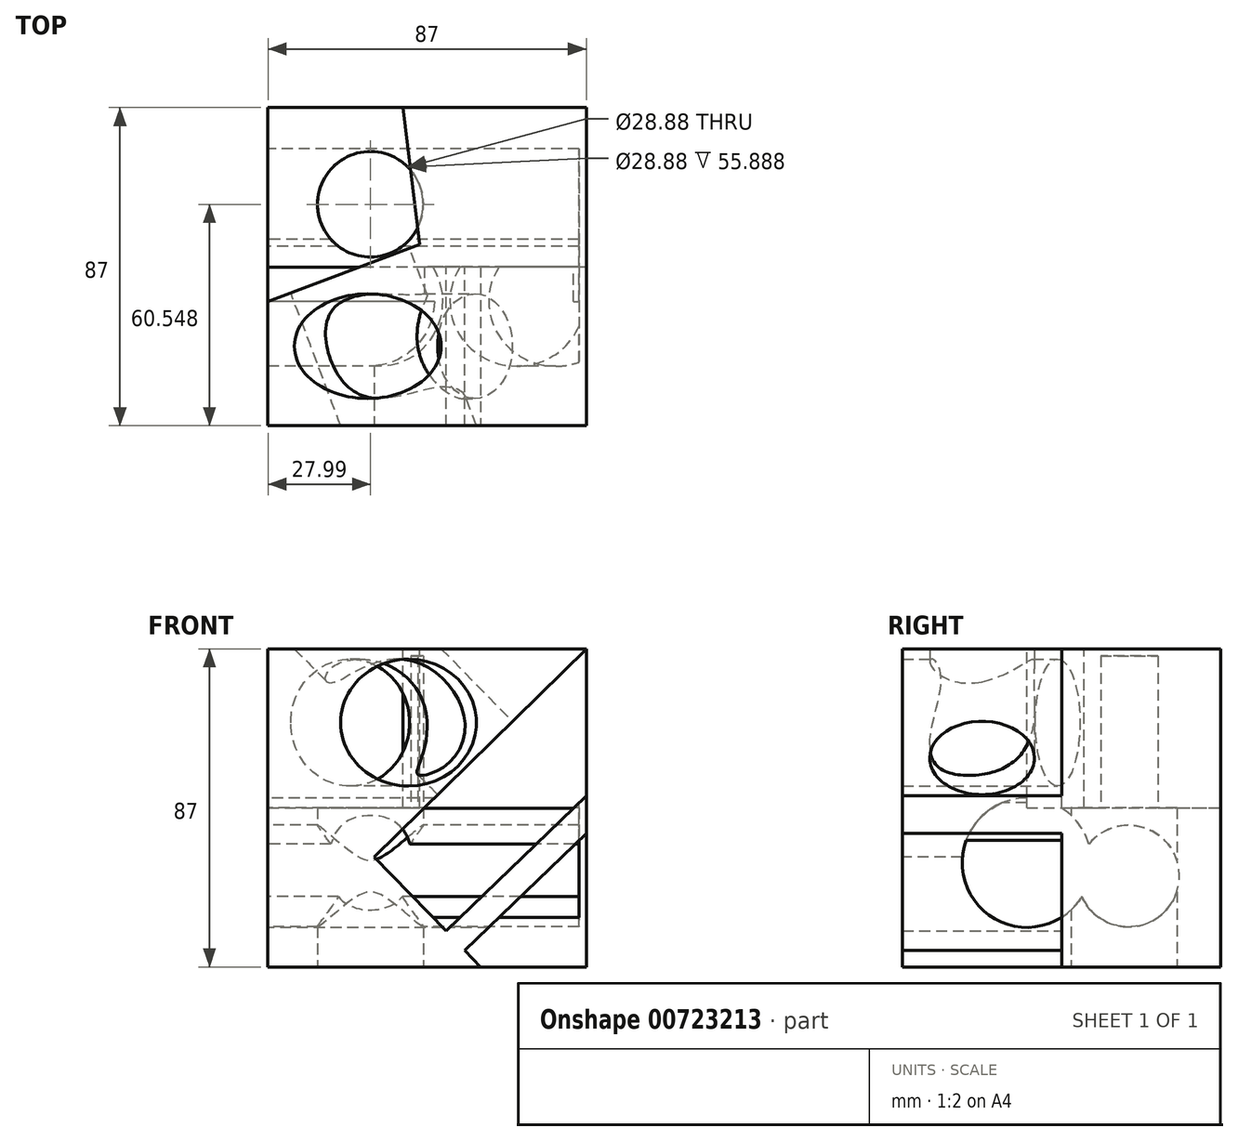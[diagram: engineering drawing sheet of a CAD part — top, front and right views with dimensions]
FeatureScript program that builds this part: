
annotation { "Feature Type Name" : "Feature", "Feature Type Description" : "" }
export const myFeature = defineFeature(function(context is Context, id is Id, definition is map)
    precondition{}
    {
        {
            var Q0;
            Q0=qCreatedBy(makeId("Front.planeOp"),FACE);
            var sketch = newSketch(context, id + "F0", { "sketchPlane" : qUnion([Q0])});
            skLineSegment(sketch, "E0.bottom", {"start": v(-41.52, 43.5) * mm, "end": v(45.48, 43.5) * mm});
            skLineSegment(sketch, "E0.top", {"start": v(-41.52, -43.5) * mm, "end": v(45.48, -43.5) * mm});
            skLineSegment(sketch, "E0.left", {"start": v(-41.52, 43.5) * mm, "end": v(-41.52, -43.5) * mm});
            skLineSegment(sketch, "E0.right", {"start": v(45.48, 43.5) * mm, "end": v(45.48, -43.5) * mm});
            skPoint(sketch, "E0.middle", {"position": v(1.98, 0) * mm});
            skSolve(sketch);
        }
        {
            var Q0;
            Q0=makeQuery(id+"F0.imprint","IMPRINT",FACE,{"disambiguationData":[TD([[makeQuery(id+"F0.imprint","IMPRINT",EDGE,{"derivedFrom":sQuery(id+"F0.wireOp",EDGE,"E0.bottom")}),-1.0]])]});
            extrude(context, id + "F1", {"entities" : qUnion([Q0]), "depth" : 87 * mm, "offsetDistance" : 25 * mm});
        }
        {
            var Q0;
            Q0=makeQuery(id+"F1.opExtrude","SWEPT_FACE",FACE,{"disambiguationData":[OSD([sQuery(id+"F0.wireOp",EDGE,"E0.bottom")])]});
            var sketch = newSketch(context, id + "F2", { "sketchPlane" : qUnion([Q0])});
            skLineSegment(sketch, "E1", {"start": v(-41.52, -53.03) * mm, "end": v(45.48, -20.33) * mm});
            skLineSegment(sketch, "E2", {"start": v(0, -37.42) * mm, "end": v(-4.6, 0) * mm});
            skSolve(sketch);
        }
        {
            var Q0;
            {var subQ4=sQuery(id+"F2.wireOp",EDGE,"E2");Q0=makeQuery(id+"F2.imprint","IMPRINT",FACE,{"disambiguationData":[TD([[makeQuery(id+"F2.imprint","IMPRINT",EDGE,{"derivedFrom":subQ4}),1.0]])]});}
            extrude(context, id + "F3", {"entities" : qUnion([Q0]), "operationType" : NewBodyOperationType.REMOVE, "oppositeDirection" : true, "depth" : 43.5 * mm, "offsetDistance" : 25 * mm});
        }
        {
            var Q0;
            Q0=makeQuery(id+"F1.opExtrude","CAP_FACE",FACE,{"disambiguationData":[OSD([sQuery(id+"F0.wireOp",EDGE,"E0.bottom"),sQuery(id+"F0.wireOp",EDGE,"E0.top"),sQuery(id+"F0.wireOp",EDGE,"E0.left"),sQuery(id+"F0.wireOp",EDGE,"E0.right")])],"isStart":false});
            var sketch = newSketch(context, id + "F4", { "sketchPlane" : qUnion([Q0])});
            skLineSegment(sketch, "E3", {"start": v(-41.52, 16.7) * mm, "end": v(16.6, -43.5) * mm});
            skLineSegment(sketch, "E4", {"start": v(-12.46, -13.4) * mm, "end": v(45.48, 43.5) * mm});
            skSolve(sketch);
        }
        {
            var Q0;
            {var subQ3=sQuery(id+"F4.wireOp",EDGE,"E4");Q0=makeQuery(id+"F4.imprint","IMPRINT",FACE,{"disambiguationData":[TD([[makeQuery(id+"F4.imprint","IMPRINT",EDGE,{"derivedFrom":subQ3}),-1.0]])]});}
            extrude(context, id + "F5", {"entities" : qUnion([Q0]), "operationType" : NewBodyOperationType.REMOVE, "oppositeDirection" : true, "depth" : 43.5 * mm, "offsetDistance" : 25 * mm});
        }
        {
            var Q0;
            Q0=makeQuery(id+"F1.opExtrude","SWEPT_FACE",FACE,{"disambiguationData":[OSD([sQuery(id+"F0.wireOp",EDGE,"E0.top")])]});
            var sketch = newSketch(context, id + "F6", { "sketchPlane" : qUnion([Q0])});
            skCircle(sketch, "E5", {"center": v(-13.53, 26.45) * mm, "radius": 14.44 * mm});
            skSolve(sketch);
        }
        {
            var Q0;
            Q0=makeQuery(id+"F6.imprint","IMPRINT",FACE,{"disambiguationData":[TD([[makeQuery(id+"F6.imprint","IMPRINT",EDGE,{"derivedFrom":sQuery(id+"F6.wireOp",EDGE,"E5")}),1.0]])]});
            extrude(context, id + "F7", {"entities" : qUnion([Q0]), "operationType" : NewBodyOperationType.REMOVE, "oppositeDirection" : true, "depth" : 85 * mm, "offsetDistance" : 25 * mm});
        }
        {
            var Q0;
            Q0=makeQuery(id+"F1.opExtrude","SWEPT_FACE",FACE,{"disambiguationData":[OSD([sQuery(id+"F0.wireOp",EDGE,"E0.left")])]});
            var sketch = newSketch(context, id + "F8", { "sketchPlane" : qUnion([Q0])});
            skCircle(sketch, "E6", {"center": v(25.25, -18.65) * mm, "radius": 13.9 * mm});
            skSolve(sketch);
        }
        {
            var Q0;
            Q0=makeQuery(id+"F8.imprint","IMPRINT",FACE,{"disambiguationData":[TD([[makeQuery(id+"F8.imprint","IMPRINT",EDGE,{"derivedFrom":sQuery(id+"F8.wireOp",EDGE,"E6")}),1.0]])]});
            extrude(context, id + "F9", {"entities" : qUnion([Q0]), "operationType" : NewBodyOperationType.REMOVE, "oppositeDirection" : true, "depth" : 85 * mm, "offsetDistance" : 25 * mm});
        }
        {
            var Q0;
            Q0=makeQuery(id+"F5.boolean.opBoolean","COPY",FACE,{"derivedFrom":makeQuery(id+"F5.opExtrude","SWEPT_FACE",FACE,{"disambiguationData":[OSD([sQuery(id+"F4.wireOp",EDGE,"E4")])]})});
            var sketch = newSketch(context, id + "F10", { "sketchPlane" : qUnion([Q0])});
            skCircle(sketch, "E7", {"center": v(20.31, 65.25) * mm, "radius": 14.31 * mm});
            skPoint(sketch, "E7.centerSnap0", {"position": v(62.93, 65.25) * mm});
            skLineSegment(sketch, "E8", {"start": v(-18.28, 65.25) * mm, "end": v(62.93, 65.25) * mm, "construction": true});
            skLineSegment(sketch, "E9", {"start": v(63, 64.77) * mm, "end": v(20.31, 65.25) * mm, "construction": true});
            skLineSegment(sketch, "E10", {"start": v(20.31, 87) * mm, "end": v(20.31, 43.5) * mm, "construction": true});
            skSolve(sketch);
        }
        {
            var Q0;
            Q0=makeQuery(id+"F10.imprint","IMPRINT",FACE,{"disambiguationData":[TD([[makeQuery(id+"F10.imprint","IMPRINT",EDGE,{"derivedFrom":sQuery(id+"F10.wireOp",EDGE,"E7")}),1.0]])]});
            extrude(context, id + "F11", {"entities" : qUnion([Q0]), "operationType" : NewBodyOperationType.REMOVE, "oppositeDirection" : true, "depth" : 87 * mm, "offsetDistance" : 25 * mm});
        }
        {
            var Q0;
            Q0=makeQuery(id+"F5.boolean.opBoolean","COPY",FACE,{"derivedFrom":makeQuery(id+"F5.opExtrude","CAP_FACE",FACE,{"disambiguationData":[OSD([sQuery(id+"F0.wireOp",EDGE,"E0.top"),sQuery(id+"F0.wireOp",EDGE,"E0.right"),sQuery(id+"F4.wireOp",EDGE,"E3"),sQuery(id+"F4.wireOp",EDGE,"E4")])],"isStart":false})});
            var sketch = newSketch(context, id + "F12", { "sketchPlane" : qUnion([Q0])});
            skLineSegment(sketch, "E11", {"start": v(7.14, -33.7) * mm, "end": v(45.48, 3.32) * mm});
            skPoint(sketch, "E11.endSnap0", {"position": v(45.48, 0) * mm});
            skLineSegment(sketch, "E12", {"start": v(12.26, -39) * mm, "end": v(45.48, -6.92) * mm});
            skLineSegment(sketch, "E13", {"start": v(45.48, -6.92) * mm, "end": v(45.48, 3.32) * mm});
            skLineSegment(sketch, "E14", {"start": v(7.14, -33.7) * mm, "end": v(12.26, -39) * mm});
            skSolve(sketch);
        }
        {
            var Q0;
            Q0=makeQuery(id+"F12.imprint","IMPRINT",FACE,{"disambiguationData":[TD([[makeQuery(id+"F12.imprint","IMPRINT",EDGE,{"derivedFrom":sQuery(id+"F12.wireOp",EDGE,"E11")}),-1.0]])]});
            extrude(context, id + "F13", {"entities" : qUnion([Q0]), "operationType" : NewBodyOperationType.ADD, "depth" : 43.5 * mm, "offsetDistance" : 25 * mm});
        }
        {
            var Q0;
            Q0=makeQuery(id+"F1.opExtrude","SWEPT_FACE",FACE,{"disambiguationData":[OSD([sQuery(id+"F0.wireOp",EDGE,"E0.left")])]});
            var sketch = newSketch(context, id + "F14", { "sketchPlane" : qUnion([Q0])});
            skCircle(sketch, "E15", {"center": v(53.03, -15) * mm, "radius": 17.71 * mm});
            skSolve(sketch);
        }
        {
            var Q0;
            {var subQ5=sQuery(id+"F14.wireOp",EDGE,"E15");var subQ7=makeQuery(id+"F9.boolean.opBoolean","COPY",EDGE,{"derivedFrom":makeQuery(id+"F9.opExtrude","CAP_EDGE",EDGE,{"disambiguationData":[OSD([sQuery(id+"F8.wireOp",EDGE,"E6")])],"isStart":true})});var subQ10=makeQuery(id+"F14.imprint","INTERSECT",VERTEX,{"disambiguationData":[OD(0.0)],"derivedFrom":[subQ7,subQ5]});Q0=makeQuery(id+"F14.imprint","IMPRINT",FACE,{"disambiguationData":[TD([[makeQuery(id+"F14.imprint","IMPRINT",EDGE,{"disambiguationData":[TD([[subQ10,1.0]])],"derivedFrom":subQ7}),-1.0]])]});}
            var Q1;
            {var subQ0=sQuery(id+"F14.wireOp",EDGE,"E15");var subQ1=sQuery(id+"F0.wireOp",EDGE,"E0.left");var subQ2=sQuery(id+"F0.wireOp",EDGE,"E0.bottom");var subQ3=makeQuery(id+"F3.boolean.opBoolean","COPY",EDGE,{"derivedFrom":makeQuery(id+"F3.opExtrude","CAP_EDGE",EDGE,{"disambiguationData":[OSD([subQ2,subQ1])],"isStart":false})});var subQ4=makeQuery(id+"F14.imprint","INTERSECT",VERTEX,{"derivedFrom":[subQ3,subQ0]});Q1=makeQuery(id+"F14.imprint","IMPRINT",FACE,{"disambiguationData":[TD([[makeQuery(id+"F14.imprint","IMPRINT",EDGE,{"disambiguationData":[TD([[subQ4,1.0]])],"derivedFrom":subQ0}),1.0]])]});}
            extrude(context, id + "F15", {"entities" : qUnion([Q0, Q1]), "operationType" : NewBodyOperationType.REMOVE, "oppositeDirection" : true, "depth" : 85 * mm, "offsetDistance" : 25 * mm});
        }
        {
            var Q0;
            Q0=makeQuery(id+"F3.boolean.opBoolean","COPY",FACE,{"derivedFrom":makeQuery(id+"F3.opExtrude","SWEPT_FACE",FACE,{"disambiguationData":[OSD([sQuery(id+"F2.wireOp",EDGE,"E1")])]})});
            var sketch = newSketch(context, id + "F16", { "sketchPlane" : qUnion([Q0])});
            skCircle(sketch, "E16", {"center": v(33.52, 23.3) * mm, "radius": 17.35 * mm});
            skSolve(sketch);
        }
        {
            var Q0;
            Q0=makeQuery(id+"F16.imprint","IMPRINT",FACE,{"disambiguationData":[TD([[makeQuery(id+"F16.imprint","IMPRINT",EDGE,{"derivedFrom":sQuery(id+"F16.wireOp",EDGE,"E16")}),1.0]])]});
            extrude(context, id + "F17", {"entities" : qUnion([Q0]), "operationType" : NewBodyOperationType.REMOVE, "oppositeDirection" : true, "depth" : 87 * mm, "offsetDistance" : 25 * mm});
        }
    });
